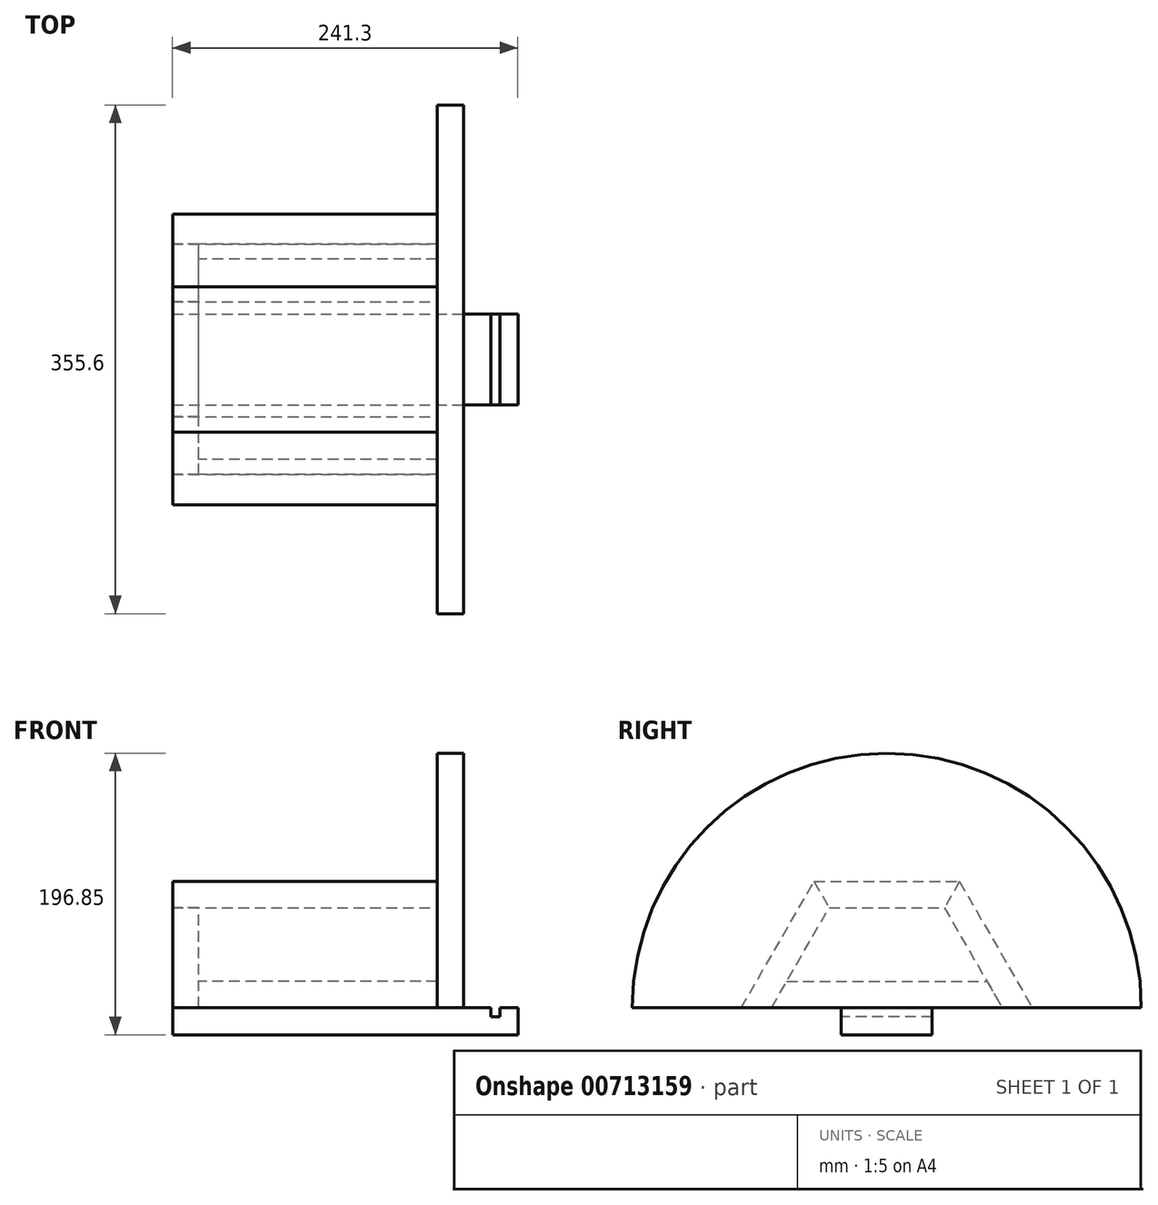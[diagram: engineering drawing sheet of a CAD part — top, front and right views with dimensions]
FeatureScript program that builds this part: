
annotation { "Feature Type Name" : "Feature", "Feature Type Description" : "" }
export const myFeature = defineFeature(function(context is Context, id is Id, definition is map)
    precondition{}
    {
        {
            var Q0;
            Q0=qCreatedBy(makeId("Right.planeOp"),FACE);
            var sketch = newSketch(context, id + "F0", { "sketchPlane" : qUnion([Q0])});
            skArc(sketch, "E0", {"start": v(177.8, 0) * mm, "mid": v(0, 177.8) * mm, "end": v(-177.8, 0) * mm});
            skLineSegment(sketch, "E1", {"start": v(-177.8, 0) * mm, "end": v(177.8, 0) * mm});
            skSolve(sketch);
        }
        {
            var Q0;
            Q0 = qSketchRegion(id + "F0", true);
            extrude(context, id + "F1", {"entities" : qUnion([Q0]), "depth" : 18.26 * mm, "offsetDistance" : 25.4 * mm});
        }
        {
            var Q0;
            Q0=makeQuery(id+"F1.opExtrude","CAP_FACE",FACE,{"disambiguationData":[OSD([sQuery(id+"F0.wireOp",EDGE,"E0"),sQuery(id+"F0.wireOp",EDGE,"E1")])],"isStart":true});
            var sketch = newSketch(context, id + "F2", { "sketchPlane" : qUnion([Q0])});
            skCircle(sketch, "E2", {"center": v(0, 0) * mm, "radius": 101.6 * mm, "construction": true});
            skLineSegment(sketch, "E3", {"start": v(0, 0) * mm, "end": v(-50.8, 87.99) * mm});
            skLineSegment(sketch, "E4", {"start": v(-50.8, 87.99) * mm, "end": v(50.8, 87.99) * mm});
            skLineSegment(sketch, "E5", {"start": v(50.8, 87.99) * mm, "end": v(101.6, 0) * mm});
            skLineSegment(sketch, "E6", {"start": v(101.6, 0) * mm, "end": v(-101.6, 0) * mm});
            skLineSegment(sketch, "E7", {"start": v(-101.6, 0) * mm, "end": v(-50.8, 87.99) * mm});
            skLineSegment(sketch, "E8", {"start": v(0, 0) * mm, "end": v(50.8, 87.99) * mm});
            skLineSegment(sketch, "E9.0", {"start": v(40.26, 69.73) * mm, "end": v(80.51, 0) * mm});
            skLineSegment(sketch, "E9.1", {"start": v(-40.26, 69.73) * mm, "end": v(40.26, 69.73) * mm});
            skLineSegment(sketch, "E9.2", {"start": v(-80.51, 0) * mm, "end": v(-40.26, 69.73) * mm});
            skSolve(sketch);
        }
        {
            var Q0;
            Q0=makeQuery(id+"F1.opExtrude","CAP_FACE",FACE,{"disambiguationData":[OSD([sQuery(id+"F0.wireOp",EDGE,"E0"),sQuery(id+"F0.wireOp",EDGE,"E1")])],"isStart":false});
            cPlane(context, id + "F3", {"entities" : qUnion([Q0]), "cplaneType" : CPlaneType.OFFSET, "offset" : 203.2 * mm, "oppositeDirection" : true, "width" : 152.4 * mm, "height" : 152.4 * mm});
        }
        {
            var Q0;
            {var subQ0=sQuery(id+"F2.wireOp",EDGE,"E7");Q0=makeQuery(id+"F2.imprint","IMPRINT",FACE,{"disambiguationData":[TD([[makeQuery(id+"F2.imprint","IMPRINT",EDGE,{"derivedFrom":subQ0}),-1.0]])]});}
            var Q1;
            {var subQ0=sQuery(id+"F2.wireOp",EDGE,"E5");Q1=makeQuery(id+"F2.imprint","IMPRINT",FACE,{"disambiguationData":[TD([[makeQuery(id+"F2.imprint","IMPRINT",EDGE,{"derivedFrom":subQ0}),-1.0]])]});}
            var Q2;
            Q2=qCreatedBy(id+"F3.planeOp",FACE);
            extrude(context, id + "F4", {"entities" : qUnion([Q0, Q1]), "endBound" : BoundingType.UP_TO_SURFACE, "depth" : 25.4 * mm, "endBoundEntityFace" : qUnion([Q2]), "offsetDistance" : 25.4 * mm});
        }
        {
            var Q0;
            {var subQ0=sQuery(id+"F2.wireOp",EDGE,"E4");Q0=makeQuery(id+"F2.imprint","IMPRINT",FACE,{"disambiguationData":[TD([[makeQuery(id+"F2.imprint","IMPRINT",EDGE,{"derivedFrom":subQ0}),-1.0]])]});}
            var Q1;
            Q1=makeQuery(id+"F4.opExtrude","CAP_FACE",FACE,{"disambiguationData":[OSD([sQuery(id+"F2.wireOp",EDGE,"E3"),sQuery(id+"F2.wireOp",EDGE,"E6"),sQuery(id+"F2.wireOp",EDGE,"E7"),sQuery(id+"F2.wireOp",EDGE,"E9.2")])],"isStart":false});
            extrude(context, id + "F5", {"entities" : qUnion([Q0]), "endBound" : BoundingType.UP_TO_SURFACE, "depth" : 25.4 * mm, "endBoundEntityFace" : qUnion([Q1]), "offsetDistance" : 25.4 * mm});
        }
        {
            var Q0;
            Q0=makeQuery(id+"F4.opExtrude","CAP_FACE",FACE,{"disambiguationData":[OSD([sQuery(id+"F2.wireOp",EDGE,"E3"),sQuery(id+"F2.wireOp",EDGE,"E6"),sQuery(id+"F2.wireOp",EDGE,"E7"),sQuery(id+"F2.wireOp",EDGE,"E9.2")])],"isStart":false});
            var sketch = newSketch(context, id + "F6", { "sketchPlane" : qUnion([Q0])});
            skLineSegment(sketch, "E10.0", {"start": v(-40.26, 69.73) * mm, "end": v(-80.51, 0) * mm});
            skLineSegment(sketch, "E11.0", {"start": v(40.26, 69.73) * mm, "end": v(-40.26, 69.73) * mm});
            skLineSegment(sketch, "E12.0", {"start": v(80.51, 0) * mm, "end": v(40.26, 69.73) * mm});
            skLineSegment(sketch, "E13.0", {"start": v(101.6, 0) * mm, "end": v(-101.6, 0) * mm});
            skSolve(sketch);
        }
        {
            var Q0;
            {var subQ0=sQuery(id+"F6.wireOp",EDGE,"E10.0");Q0=makeQuery(id+"F6.imprint","IMPRINT",FACE,{"disambiguationData":[TD([[makeQuery(id+"F6.imprint","IMPRINT",EDGE,{"derivedFrom":subQ0}),1.0]])]});}
            extrude(context, id + "F7", {"entities" : qUnion([Q0]), "oppositeDirection" : true, "depth" : 18.26 * mm, "offsetDistance" : 25.4 * mm});
        }
        {
            var Q0;
            Q0=makeQuery(id+"F7.opExtrude","CAP_FACE",FACE,{"disambiguationData":[OSD([sQuery(id+"F6.wireOp",EDGE,"E10.0"),sQuery(id+"F6.wireOp",EDGE,"E11.0"),sQuery(id+"F6.wireOp",EDGE,"E12.0"),sQuery(id+"F6.wireOp",EDGE,"E13.0")])],"isStart":false});
            var sketch = newSketch(context, id + "F8", { "sketchPlane" : qUnion([Q0])});
            skLineSegment(sketch, "E14.0.0", {"start": v(-80.51, 0) * mm, "end": v(80.51, 0) * mm});
            skLineSegment(sketch, "E14.0.1", {"start": v(80.51, 0) * mm, "end": v(40.26, 69.73) * mm});
            skLineSegment(sketch, "E14.0.2", {"start": v(40.26, 69.73) * mm, "end": v(-40.26, 69.73) * mm});
            skLineSegment(sketch, "E14.0.3", {"start": v(-40.26, 69.73) * mm, "end": v(-80.51, 0) * mm});
            skLineSegment(sketch, "E15", {"start": v(-69.97, 18.26) * mm, "end": v(69.97, 18.26) * mm});
            skSolve(sketch);
        }
        {
            var Q0;
            {var subQ0=sQuery(id+"F8.wireOp",EDGE,"E14.0.0");Q0=makeQuery(id+"F8.imprint","IMPRINT",FACE,{"disambiguationData":[TD([[makeQuery(id+"F8.imprint","IMPRINT",EDGE,{"derivedFrom":subQ0}),1.0]])]});}
            var Q1;
            Q1=makeQuery(id+"F1.opExtrude","CAP_FACE",FACE,{"disambiguationData":[OSD([sQuery(id+"F0.wireOp",EDGE,"E0"),sQuery(id+"F0.wireOp",EDGE,"E1")])],"isStart":true});
            extrude(context, id + "F9", {"entities" : qUnion([Q0]), "endBound" : BoundingType.UP_TO_SURFACE, "depth" : 25.4 * mm, "endBoundEntityFace" : qUnion([Q1]), "offsetDistance" : 25.4 * mm});
        }
        {
            var Q0;
            Q0=makeQuery(id+"F9.opExtrude","SWEPT_FACE",FACE,{"disambiguationData":[OSD([sQuery(id+"F8.wireOp",EDGE,"E14.0.0")])]});
            var sketch = newSketch(context, id + "F10", { "sketchPlane" : qUnion([Q0])});
            skLineSegment(sketch, "E16.0.0", {"start": v(-184.94, 80.51) * mm, "end": v(-184.94, -80.51) * mm, "construction": true});
            skLineSegment(sketch, "E16.0.1", {"start": v(-184.94, -80.51) * mm, "end": v(-166.67, -80.51) * mm, "construction": true});
            skLineSegment(sketch, "E16.0.2", {"start": v(-166.67, -80.51) * mm, "end": v(-166.67, 80.51) * mm, "construction": true});
            skLineSegment(sketch, "E16.0.3", {"start": v(-166.67, 80.51) * mm, "end": v(-184.94, 80.51) * mm, "construction": true});
            skLineSegment(sketch, "E17.bottom", {"start": v(-184.94, -31.75) * mm, "end": v(56.36, -31.75) * mm});
            skLineSegment(sketch, "E17.top", {"start": v(-184.94, 31.75) * mm, "end": v(56.36, 31.75) * mm});
            skLineSegment(sketch, "E17.left", {"start": v(-184.94, -31.75) * mm, "end": v(-184.94, 31.75) * mm});
            skLineSegment(sketch, "E17.right", {"start": v(56.36, -31.75) * mm, "end": v(56.36, 31.75) * mm});
            skLineSegment(sketch, "E18", {"start": v(0, 0) * mm, "end": v(56.36, 0) * mm, "construction": true});
            skSolve(sketch);
        }
        {
            var Q0;
            Q0 = qSketchRegion(id + "F10", true);
            extrude(context, id + "F11", {"entities" : qUnion([Q0]), "depth" : 19.05 * mm, "offsetDistance" : 25.4 * mm});
        }
        {
            var Q0;
            Q0=makeQuery(id+"F11.opExtrude","SWEPT_FACE",FACE,{"disambiguationData":[OSD([sQuery(id+"F10.wireOp",EDGE,"E17.top")])]});
            var sketch = newSketch(context, id + "F12", { "sketchPlane" : qUnion([Q0])});
            skLineSegment(sketch, "E19.bottom", {"start": v(37.31, 0) * mm, "end": v(43.66, 0) * mm});
            skLineSegment(sketch, "E19.top", {"start": v(37.31, -6.35) * mm, "end": v(43.66, -6.35) * mm});
            skLineSegment(sketch, "E19.left", {"start": v(37.31, 0) * mm, "end": v(37.31, -6.35) * mm});
            skLineSegment(sketch, "E19.right", {"start": v(43.66, 0) * mm, "end": v(43.66, -6.35) * mm});
            skSolve(sketch);
        }
        {
            var Q0;
            Q0 = qSketchRegion(id + "F12", true);
            extrude(context, id + "F13", {"entities" : qUnion([Q0]), "operationType" : NewBodyOperationType.REMOVE, "endBound" : BoundingType.THROUGH_ALL, "oppositeDirection" : true, "depth" : 25.4 * mm, "offsetDistance" : 25.4 * mm});
        }
    });
